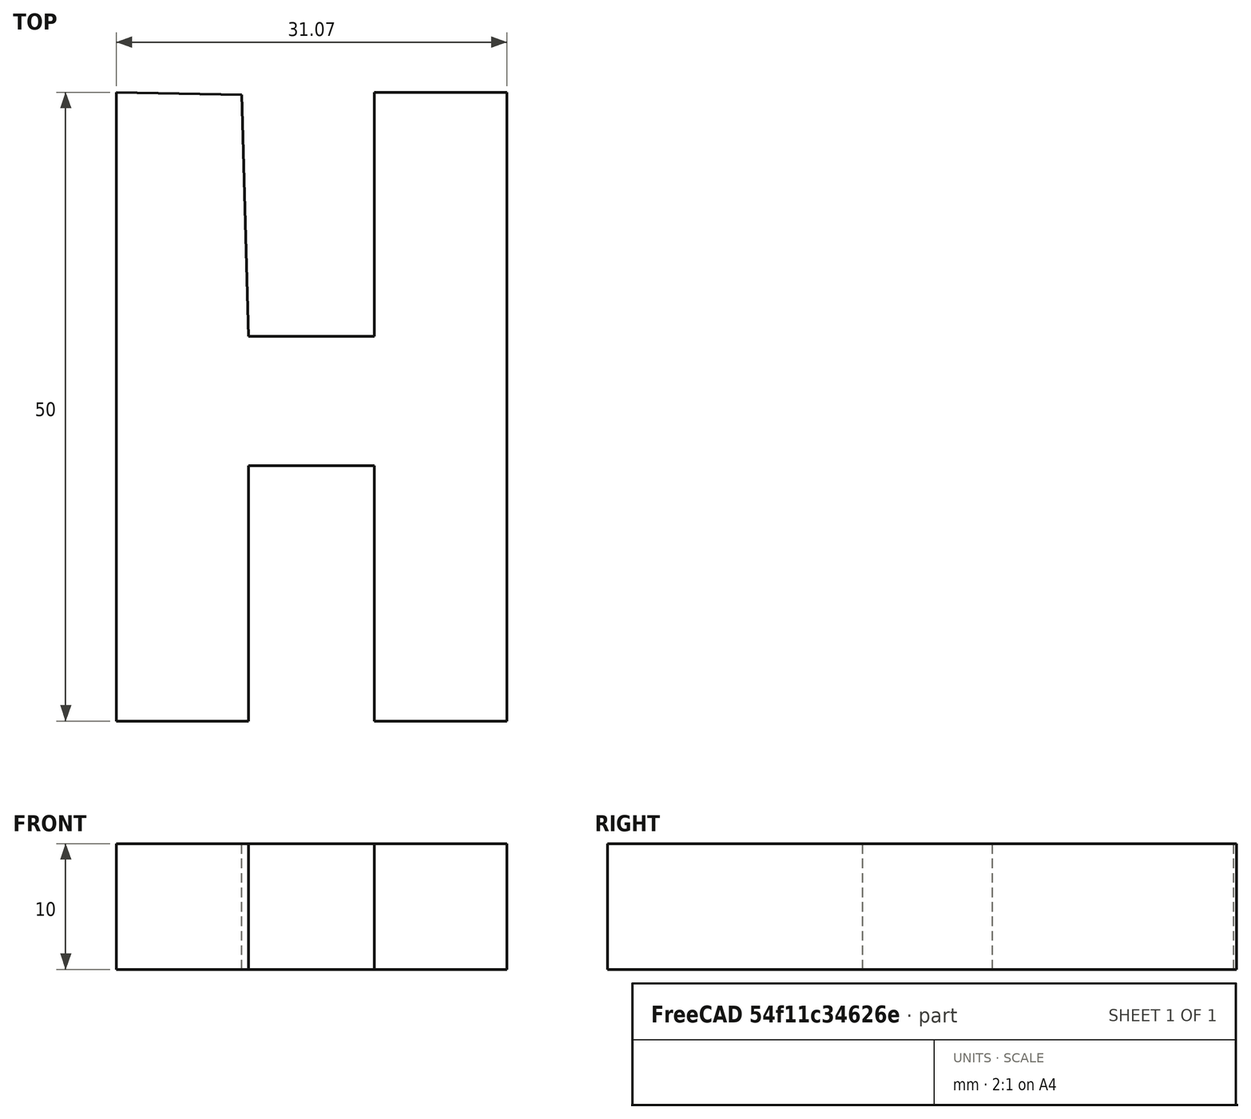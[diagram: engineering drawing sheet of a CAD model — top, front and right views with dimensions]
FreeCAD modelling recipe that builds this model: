
FCSTD DOCUMENT  (FreeCAD 0.21R33694 (Git))
Label: OJT1_T18R02_hola
License: All rights reserved
LicenseURL: http://en.wikipedia.org/wiki/All_rights_reserved
objects: Sketcher::SketchObject×4, PartDesign::Pad×1, PartDesign::Body×1
note: 7 computed .brp shape members not serialized (recipe doc carries the construction recipe); baked Part::Feature solids carry a one-line shape summary decoded from their .brp

FEATURE [Sketcher::SketchObject] Sketch  label="lletra h"
  FullyConstrained = true
  MapMode = 5
  Support = -> [XY_Plane]
  sketch-geometry (12):
    g0: LineSegment StartX=0 StartY=50 StartZ=0 EndX=0 EndY=0 EndZ=0
    g1: LineSegment StartX=0 StartY=0 StartZ=0 EndX=10.5338 EndY=0 EndZ=0
    g2: LineSegment StartX=10.5338 StartY=0 StartZ=0 EndX=10.5338 EndY=20.303 EndZ=0
    g3: LineSegment StartX=10.5338 StartY=20.303 StartZ=0 EndX=20.5338 EndY=20.303 EndZ=0
    g4: LineSegment StartX=20.5338 StartY=20.303 StartZ=0 EndX=20.5338 EndY=0 EndZ=0
    g5: LineSegment StartX=20.5338 StartY=0 StartZ=0 EndX=31.0677 EndY=0 EndZ=0
    g6: LineSegment StartX=31.0677 StartY=0 StartZ=0 EndX=31.0677 EndY=50 EndZ=0
    g7: LineSegment StartX=31.0677 StartY=50 StartZ=0 EndX=20.5338 EndY=50 EndZ=0
    g8: LineSegment StartX=20.5338 StartY=50 StartZ=0 EndX=20.5338 EndY=30.6061 EndZ=0
    g9: LineSegment StartX=20.5338 StartY=30.6061 StartZ=0 EndX=10.5338 EndY=30.6061 EndZ=0
    g10: LineSegment StartX=10.5338 StartY=30.6061 StartZ=0 EndX=10 EndY=49.798 EndZ=0
    g11: LineSegment StartX=10 StartY=49.798 StartZ=0 EndX=0 EndY=50 EndZ=0
  constraints (34):
    c: PointOnObject(g0,g-2)
    c: Coincident(g0,g-1)
    c: Coincident(g0,g1)
    c: PointOnObject(g1,g-1)
    c: Coincident(g1,g2)
    c: Vertical(g2)
    c: Coincident(g2,g3)
    c: Coincident(g3,g4)
    c: PointOnObject(g4,g-1)
    c: Vertical(g4)
    c: Coincident(g4,g5)
    c: Coincident(g5,g6)
    c: Vertical(g6)
    c: Coincident(g6,g7)
    c: Coincident(g7,g8)
    c: Vertical(g8)
    c: Coincident(g8,g9)
    c: Coincident(g9,g10)
    c: Coincident(g10,g11)
    c: Coincident(g11,g0)
    c: DistanceY(g0,g0) = 50
    c: DistanceX(g11,g11) = 10
    c: Equal(g7,g1)
    c: Equal(g1,g5)
    c: Horizontal(g9)
    c: Horizontal(g3)
    c: DistanceX(g9,g9) = 10
    c: Equal(g9,g3)
    c: Equal(g0,g6)
    c: Horizontal(g5)
    c: Horizontal(g7)
    c: Block(g1)
    c: Block(g2)
    c: Block(g10)
FEATURE [Sketcher::SketchObject] Sketch002  label="lletra l"
  FullyConstrained = true
  MapMode = 5
  Support = -> [XY_Plane]
  sketch-geometry (6):
    g0: LineSegment StartX=100.156 StartY=50 StartZ=0 EndX=100.156 EndY=0 EndZ=0
    g1: LineSegment StartX=100.156 StartY=0 StartZ=0 EndX=130.156 EndY=0 EndZ=0
    g2: LineSegment StartX=130.156 StartY=0 StartZ=0 EndX=130.156 EndY=10 EndZ=0
    g3: LineSegment StartX=130.156 StartY=10 StartZ=0 EndX=110.156 EndY=10 EndZ=0
    g4: LineSegment StartX=110.156 StartY=10 StartZ=0 EndX=110.156 EndY=50 EndZ=0
    g5: LineSegment StartX=110.156 StartY=50 StartZ=0 EndX=100.156 EndY=50 EndZ=0
  constraints (18):
    c: PointOnObject(g0,g-1)
    c: Vertical(g0)
    c: Coincident(g0,g1)
    c: Coincident(g1,g2)
    c: Coincident(g2,g3)
    c: Horizontal(g3)
    c: Coincident(g3,g4)
    c: Vertical(g4)
    c: Coincident(g4,g5)
    c: Coincident(g5,g0)
    c: Horizontal(g5)
    c: Vertical(g2)
    c: Horizontal(g1)
    c: DistanceX(g5,g5) = 10
    c: DistanceY(g0,g0) = 50
    c: DistanceX(g1,g1) = 30
    c: Equal(g5,g2)
    c: Block(g0)
FEATURE [Sketcher::SketchObject] Sketch003
  FullyConstrained = true
  MapMode = 5
  Support = -> [XY_Plane]
  sketch-geometry (12):
    g0: LineSegment StartX=149.646 StartY=0 StartZ=0 EndX=149.646 EndY=50 EndZ=0
    g1: LineSegment StartX=149.646 StartY=50 StartZ=0 EndX=179.646 EndY=50 EndZ=0
    g2: LineSegment StartX=179.646 StartY=50 StartZ=0 EndX=179.646 EndY=0 EndZ=0
    g3: LineSegment StartX=179.646 StartY=0 StartZ=0 EndX=169.546 EndY=0 EndZ=0
    g4: LineSegment StartX=169.546 StartY=0 StartZ=0 EndX=169.546 EndY=20 EndZ=0
    g5: LineSegment StartX=169.546 StartY=20 StartZ=0 EndX=159.746 EndY=20 EndZ=0
    g6: LineSegment StartX=159.746 StartY=20 StartZ=0 EndX=159.746 EndY=0 EndZ=0
    g7: LineSegment StartX=159.746 StartY=0 StartZ=0 EndX=149.646 EndY=0 EndZ=0
    g8: LineSegment StartX=160.161 StartY=39.8623 StartZ=0 EndX=160.161 EndY=29.8623 EndZ=0
    g9: LineSegment StartX=160.161 StartY=29.8623 StartZ=0 EndX=170.161 EndY=29.8623 EndZ=0
    g10: LineSegment StartX=170.161 StartY=29.8623 StartZ=0 EndX=170.161 EndY=39.8623 EndZ=0
    g11: LineSegment StartX=170.161 StartY=39.8623 StartZ=0 EndX=160.161 EndY=39.8623 EndZ=0
  constraints (35):
    c: Vertical(g0)
    c: Coincident(g0,g1)
    c: Horizontal(g1)
    c: Coincident(g1,g2)
    c: PointOnObject(g2,g-1)
    c: Vertical(g2)
    c: Coincident(g2,g3)
    c: Coincident(g3,g4)
    c: Vertical(g4)
    c: Coincident(g4,g5)
    c: Horizontal(g5)
    c: Coincident(g5,g6)
    c: PointOnObject(g6,g-1)
    c: Vertical(g6)
    c: Coincident(g6,g7)
    c: Coincident(g7,g0)
    c: Vertical(g8)
    c: Coincident(g8,g9)
    c: Horizontal(g9)
    c: Coincident(g9,g10)
    c: Vertical(g10)
    c: Coincident(g10,g11)
    c: Coincident(g11,g8)
    c: DistanceX(g1,g1) = 30
    c: DistanceY(g0,g0) = 50
    c: Horizontal(g7)
    c: Horizontal(g3)
    c: Horizontal(g11)
    c: DistanceY(g4,g4) = 20
    c: DistanceX(g7,g7) = 10.1
    c: DistanceX(g3,g3) = 10.1
    c: DistanceX(g11,g11) = 10
    c: DistanceY(g8,g8) = 10
    c: Block(g0)
    c: Block(g11)
FEATURE [PartDesign::Pad] Pad
  Direction = (0,0,1)
  Length = 10
  Length2 = 10
  Profile = -> Sketch
  ReferenceAxis = -> Sketch [N_Axis]
  Type = 0
FEATURE [Sketcher::SketchObject] Sketch004
  FullyConstrained = true
  MapMode = 5
  Support = -> [XY_Plane]
  sketch-geometry (4):
    g0: LineSegment StartX=50.7266 StartY=50 StartZ=0 EndX=50.7266 EndY=0 EndZ=0
    g1: LineSegment StartX=50.7266 StartY=0 StartZ=0 EndX=80.7266 EndY=0 EndZ=0
    g2: LineSegment StartX=80.7266 StartY=0 StartZ=0 EndX=80.7266 EndY=50 EndZ=0
    g3: LineSegment StartX=80.7266 StartY=50 StartZ=0 EndX=50.7266 EndY=50 EndZ=0
  constraints (12):
    c: Vertical(g0)
    c: Coincident(g0,g1)
    c: PointOnObject(g1,g-1)
    c: Horizontal(g1)
    c: Coincident(g1,g2)
    c: Vertical(g2)
    c: Coincident(g2,g3)
    c: Coincident(g3,g0)
    c: Horizontal(g3)
    c: DistanceX(g3,g3) = 30
    c: Equal(g3,g1)
    c: DistanceY(g2,g2) = 50
FEATURE [PartDesign::Body] Body
  Group = -> [Sketch,Sketch002,Sketch003,Pad,Sketch004]
  Origin = -> Origin
  Tip = -> Pad
